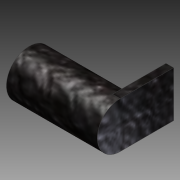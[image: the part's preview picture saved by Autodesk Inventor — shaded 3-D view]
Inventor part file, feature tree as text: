
AUTODESK INVENTOR PART (.ipt)
format: ipt  version: 2012 (Build 160160000, 160)  size: 95,744 bytes
history: native  units: mm
features: extrude x2, sketch x1
ambient origin geometry x8: Origin, YZ Plane, XZ Plane, XY Plane, X Axis, Y Axis, Z Axis, Center Point
bodies: Solid1 (feature_tree)
feature tree (3):
  sketch  "Sketch2"  dims[d0=6.0mm d2=11.9mm d3=0.0mm d7=7.0mm d8=1.0mm d9=0.0mm]
  extrude  "Extrusion1"  Depth=11.9mm TaperAngle=0.0deg
  extrude  "Extrusion3"  Depth=7.0mm
